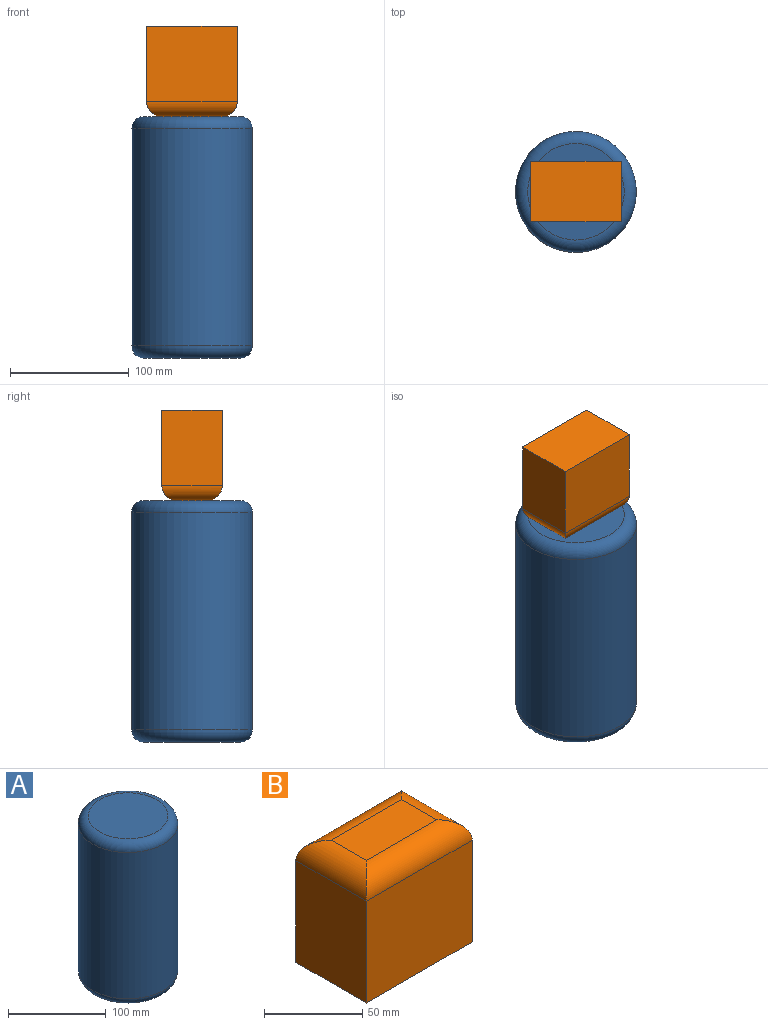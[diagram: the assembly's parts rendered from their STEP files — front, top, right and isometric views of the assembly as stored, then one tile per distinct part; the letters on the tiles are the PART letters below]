
ASSEMBLY  parts=2 mates=1
PART A: 7 faces, bbox 110x110x203.2 mm
  f0: cylinder r=50.8mm len=182.88mm, axis (0,0,-1), area 58372.7mm2, adj f3,f4
  f1: plane 81.28x81.28mm, normal (0,0,1), area 5188.7mm2, adj f4
  f2: plane 81.28x81.28mm, normal (0,0,-1), area 5152.8mm2, adj f3,f5
  f3: torus R=40.64mm, axis (0,0,1), area 4723.8mm2, adj f0,f2
  f4: torus R=40.64mm, axis (0,0,1), area 4723.8mm2, adj f0,f1
  f5: cylinder r=3.38mm len=12.7mm, axis (0,0,-1), area 269.6mm2, adj f2,f6
  f6: cone r=0mm half-angle=59deg, axis (0,0,-1), area 41.8mm2, adj f5
PART B: 10 faces, bbox 76.2x50.8x76.2 mm
  f0: plane 63.5x50.8mm, normal (1,0,0), area 3225.8mm2, adj f1,f3,f5,f6
  f1: plane 76.2x63.5mm, normal (0,1,0), area 4838.7mm2, adj f0,f2,f5,f8
  f2: plane 63.5x50.8mm, normal (-1,0,0), area 3225.8mm2, adj f1,f3,f5,f9
  f3: plane 76.2x63.5mm, normal (0,-1,0), area 4838.7mm2, adj f0,f2,f5,f7
  f4: plane 50.8x25.4mm, normal (0,0,1), area 1290.3mm2, adj f6,f7,f8,f9
  f5: plane 76.2x50.8mm, normal (0,0,-1), area 3871mm2, adj f0,f1,f2,f3
  f6: cylinder r=12.7mm len=50.8mm, axis (0,-1,0), area 829.3mm2, adj f0,f4,f7,f8
  f7: cylinder r=12.7mm len=76.2mm, axis (-1,0,0), area 1336mm2, adj f3,f4,f6,f9
  f8: cylinder r=12.7mm len=76.2mm, axis (1,0,0), area 1336mm2, adj f1,f4,f6,f9
  f9: cylinder r=12.7mm len=50.8mm, axis (0,1,0), area 829.3mm2, adj f2,f4,f7,f8
PLACE A t=(-131.62,-6.62,2.46)mm fixed
PLACE B rot(axis=(1,0,0),180deg) t=(-131.62,-6.62,281.86)mm
MATE planar B.f4 <-> A.f0  axis (0,0,-1) through (-131.62,-6.62,205.66)mm
